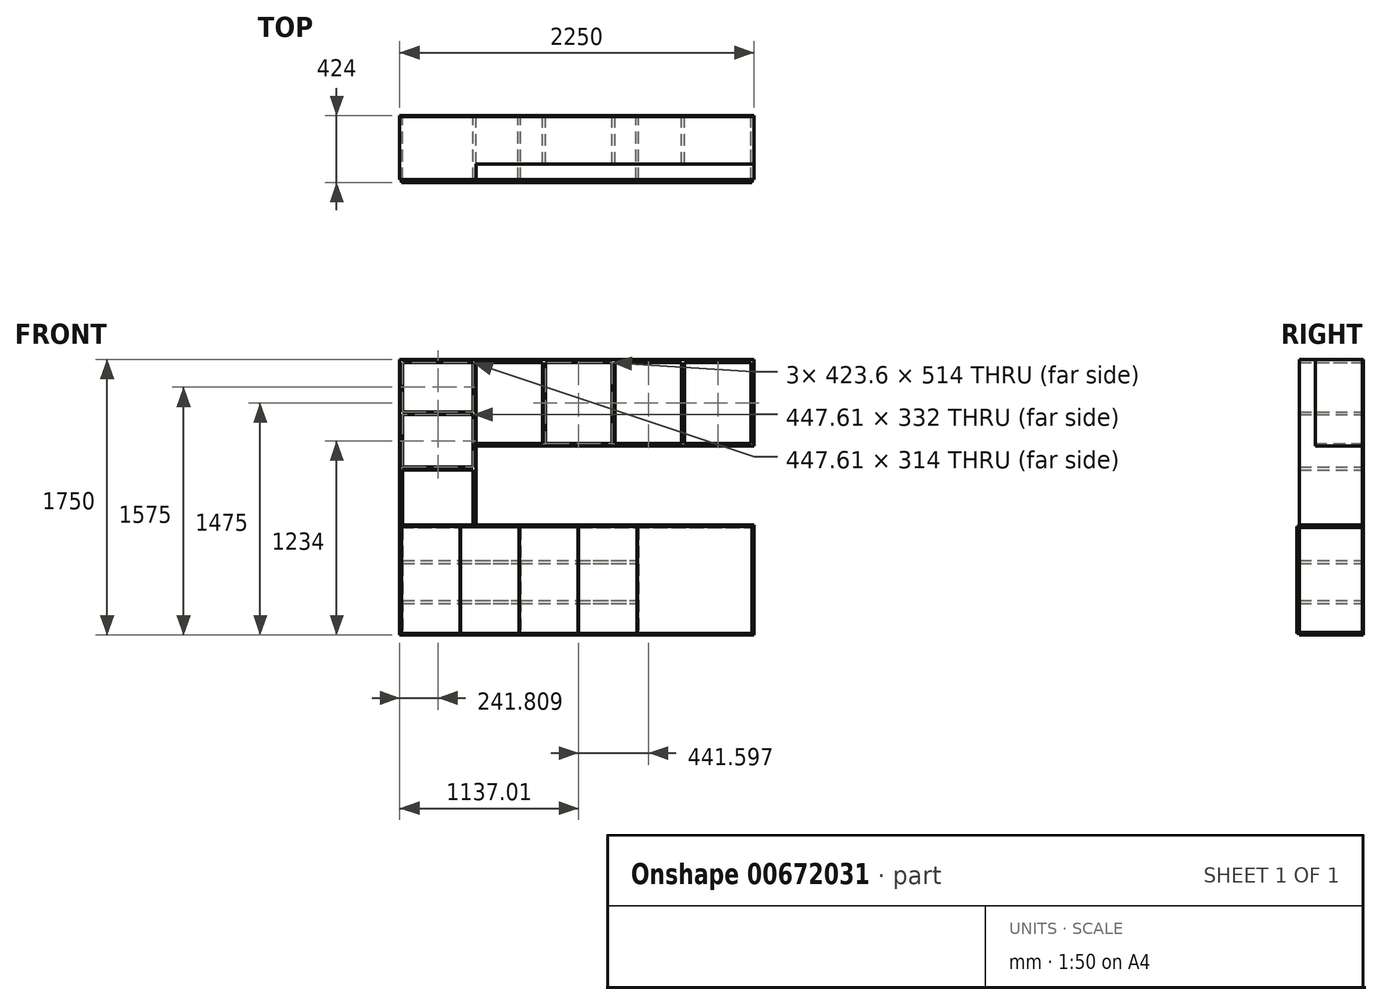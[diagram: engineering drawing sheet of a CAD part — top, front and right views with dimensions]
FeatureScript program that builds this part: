
annotation { "Feature Type Name" : "Feature", "Feature Type Description" : "" }
export const myFeature = defineFeature(function(context is Context, id is Id, definition is map)
    precondition{}
    {
        {
            var Q0;
            Q0=qCreatedBy(makeId("Front.planeOp"),FACE);
            var sketch = newSketch(context, id + "F0", { "sketchPlane" : qUnion([Q0])});
            skLineSegment(sketch, "E0.bottom", {"start": v(-1256.64, 283.33) * mm, "end": v(993.36, 283.33) * mm});
            skLineSegment(sketch, "E0.top", {"start": v(-1256.64, -416.67) * mm, "end": v(993.36, -416.67) * mm});
            skLineSegment(sketch, "E0.left", {"start": v(-1256.64, 283.33) * mm, "end": v(-1256.64, -416.67) * mm});
            skLineSegment(sketch, "E0.right", {"start": v(993.36, 283.33) * mm, "end": v(993.36, -416.67) * mm});
            skLineSegment(sketch, "E1.0", {"start": v(-1238.64, 265.33) * mm, "end": v(-1238.64, -398.67) * mm});
            skLineSegment(sketch, "E2.0", {"start": v(975.36, 265.33) * mm, "end": v(975.36, -398.67) * mm});
            skLineSegment(sketch, "E3.0", {"start": v(-1256.64, -398.67) * mm, "end": v(975.36, -398.67) * mm});
            skLineSegment(sketch, "E4.0", {"start": v(-1256.64, 265.33) * mm, "end": v(975.36, 265.33) * mm});
            skLineSegment(sketch, "E5", {"start": v(243.36, 265.33) * mm, "end": v(243.36, -398.67) * mm});
            skLineSegment(sketch, "E6.0", {"start": v(261.36, 265.33) * mm, "end": v(261.36, -398.67) * mm});
            skLineSegment(sketch, "E7", {"start": v(-1238.64, 57.6) * mm, "end": v(-506.64, 57.6) * mm});
            skLineSegment(sketch, "E8", {"start": v(-1238.64, -197.11) * mm, "end": v(-506.64, -197.11) * mm});
            skLineSegment(sketch, "E9", {"start": v(-506.64, 265.33) * mm, "end": v(-506.64, 265.33) * mm});
            skLineSegment(sketch, "E10", {"start": v(-506.64, 265.33) * mm, "end": v(-506.64, -398.67) * mm});
            skLineSegment(sketch, "E11.0", {"start": v(-488.64, 265.33) * mm, "end": v(-488.64, -398.67) * mm});
            skLineSegment(sketch, "E12.0", {"start": v(-1238.64, 39.6) * mm, "end": v(-506.64, 39.6) * mm});
            skLineSegment(sketch, "E13.0", {"start": v(-1238.64, -215.11) * mm, "end": v(-506.64, -215.11) * mm});
            skLineSegment(sketch, "E14.trimOffspring", {"start": v(-488.64, 57.6) * mm, "end": v(243.36, 57.6) * mm});
            skLineSegment(sketch, "E15.trimOffspring", {"start": v(-488.64, 39.6) * mm, "end": v(243.36, 39.6) * mm});
            skLineSegment(sketch, "E16.trimOffspring", {"start": v(-488.64, -197.11) * mm, "end": v(243.36, -197.11) * mm});
            skLineSegment(sketch, "E17.trimOffspring", {"start": v(-488.64, -215.11) * mm, "end": v(243.36, -215.11) * mm});
            skLineSegment(sketch, "E18", {"start": v(975.36, 265.33) * mm, "end": v(993.36, 265.33) * mm});
            skLineSegment(sketch, "E19", {"start": v(975.36, -398.67) * mm, "end": v(993.36, -398.67) * mm});
            skSolve(sketch);
        }
        {
            var Q0;
            {var subQ4=sQuery(id+"F0.wireOp",EDGE,"E0.bottom");Q0=makeQuery(id+"F0.imprint","IMPRINT",FACE,{"disambiguationData":[TD([[makeQuery(id+"F0.imprint","IMPRINT",EDGE,{"derivedFrom":subQ4}),-1.0]])]});}
            extrude(context, id + "F1", {"entities" : qUnion([Q0]), "depth" : 400 * mm, "offsetDistance" : 25 * mm});
        }
        {
            var Q0;
            {var subQ1=sQuery(id+"F0.wireOp",EDGE,"E0.top");Q0=makeQuery(id+"F0.imprint","IMPRINT",FACE,{"disambiguationData":[TD([[makeQuery(id+"F0.imprint","IMPRINT",EDGE,{"derivedFrom":subQ1}),1.0]])]});}
            extrude(context, id + "F2", {"entities" : qUnion([Q0]), "depth" : 400 * mm, "offsetDistance" : 25 * mm});
        }
        {
            var Q0;
            {var subQ5=sQuery(id+"F0.wireOp",EDGE,"E0.left");var subQ8=sQuery(id+"F0.wireOp",EDGE,"E3.0");var subQ9=makeQuery(id+"F0.imprint","INTERSECT",VERTEX,{"derivedFrom":[subQ5,subQ8]});Q0=makeQuery(id+"F0.imprint","IMPRINT",FACE,{"disambiguationData":[TD([[makeQuery(id+"F0.imprint","IMPRINT",EDGE,{"disambiguationData":[TD([[subQ9,1.0]])],"derivedFrom":subQ5}),1.0]])]});}
            extrude(context, id + "F3", {"entities" : qUnion([Q0]), "depth" : 400 * mm, "offsetDistance" : 25 * mm});
        }
        {
            var Q0;
            {var subQ5=sQuery(id+"F0.wireOp",EDGE,"E2.0");Q0=makeQuery(id+"F0.imprint","IMPRINT",FACE,{"disambiguationData":[TD([[makeQuery(id+"F0.imprint","IMPRINT",EDGE,{"derivedFrom":subQ5}),1.0]])]});}
            extrude(context, id + "F4", {"entities" : qUnion([Q0]), "depth" : 400 * mm, "offsetDistance" : 25 * mm});
        }
        {
            var Q0;
            {var subQ6=sQuery(id+"F0.wireOp",EDGE,"E10");var subQ7=sQuery(id+"F0.wireOp",EDGE,"E3.0");var subQ8=makeQuery(id+"F0.imprint","INTERSECT",VERTEX,{"derivedFrom":[subQ7,subQ6]});Q0=makeQuery(id+"F0.imprint","IMPRINT",FACE,{"disambiguationData":[TD([[makeQuery(id+"F0.imprint","IMPRINT",EDGE,{"disambiguationData":[TD([[subQ8,-1.0]])],"derivedFrom":subQ7}),1.0]])]});}
            extrude(context, id + "F5", {"entities" : qUnion([Q0]), "depth" : 400 * mm, "offsetDistance" : 25 * mm});
        }
        {
            var Q0;
            {var subQ0=sQuery(id+"F0.wireOp",EDGE,"E8");Q0=makeQuery(id+"F0.imprint","IMPRINT",FACE,{"disambiguationData":[TD([[makeQuery(id+"F0.imprint","IMPRINT",EDGE,{"derivedFrom":subQ0}),-1.0]])]});}
            extrude(context, id + "F6", {"entities" : qUnion([Q0]), "depth" : 400 * mm, "offsetDistance" : 25 * mm});
        }
        {
            var Q0;
            {var subQ0=sQuery(id+"F0.wireOp",EDGE,"E7");Q0=makeQuery(id+"F0.imprint","IMPRINT",FACE,{"disambiguationData":[TD([[makeQuery(id+"F0.imprint","IMPRINT",EDGE,{"derivedFrom":subQ0}),-1.0]])]});}
            extrude(context, id + "F7", {"entities" : qUnion([Q0]), "depth" : 400 * mm, "offsetDistance" : 25 * mm});
        }
        {
            var Q0;
            {var subQ0=sQuery(id+"F0.wireOp",EDGE,"E14.trimOffspring");Q0=makeQuery(id+"F0.imprint","IMPRINT",FACE,{"disambiguationData":[TD([[makeQuery(id+"F0.imprint","IMPRINT",EDGE,{"derivedFrom":subQ0}),-1.0]])]});}
            extrude(context, id + "F8", {"entities" : qUnion([Q0]), "depth" : 400 * mm, "offsetDistance" : 25 * mm});
        }
        {
            var Q0;
            {var subQ0=sQuery(id+"F0.wireOp",EDGE,"E16.trimOffspring");Q0=makeQuery(id+"F0.imprint","IMPRINT",FACE,{"disambiguationData":[TD([[makeQuery(id+"F0.imprint","IMPRINT",EDGE,{"derivedFrom":subQ0}),-1.0]])]});}
            extrude(context, id + "F9", {"entities" : qUnion([Q0]), "depth" : 400 * mm, "offsetDistance" : 25 * mm});
        }
        {
            var Q0;
            {var subQ5=sQuery(id+"F0.wireOp",EDGE,"E6.0");Q0=makeQuery(id+"F0.imprint","IMPRINT",FACE,{"disambiguationData":[TD([[makeQuery(id+"F0.imprint","IMPRINT",EDGE,{"derivedFrom":subQ5}),-1.0]])]});}
            extrude(context, id + "F10", {"entities" : qUnion([Q0]), "depth" : 400 * mm, "offsetDistance" : 25 * mm});
        }
        {
            var Q0;
            Q0=makeQuery(id+"F1.opExtrude","CAP_FACE",FACE,{"disambiguationData":[OSD([sQuery(id+"F0.wireOp",EDGE,"E0.bottom"),sQuery(id+"F0.wireOp",EDGE,"E0.left"),sQuery(id+"F0.wireOp",EDGE,"E0.right"),sQuery(id+"F0.wireOp",EDGE,"E4.0"),sQuery(id+"F0.wireOp",EDGE,"E18")])],"isStart":true});
            var sketch = newSketch(context, id + "F11", { "sketchPlane" : qUnion([Q0])});
            skLineSegment(sketch, "E20.bottom", {"start": v(-993.36, 283.33) * mm, "end": v(1256.64, 283.33) * mm});
            skLineSegment(sketch, "E20.top", {"start": v(-993.36, -416.67) * mm, "end": v(1256.64, -416.67) * mm});
            skLineSegment(sketch, "E20.left", {"start": v(1256.64, 283.33) * mm, "end": v(1256.64, -416.67) * mm});
            skLineSegment(sketch, "E20.right", {"start": v(-993.36, 283.33) * mm, "end": v(-993.36, -416.67) * mm});
            skSolve(sketch);
        }
        {
            var Q0;
            Q0 = qSketchRegion(id + "F11", true);
            extrude(context, id + "F12", {"entities" : qUnion([Q0]), "depth" : 6 * mm, "offsetDistance" : 25 * mm});
        }
        {
            var Q0;
            Q0=makeQuery(id+"F3.opExtrude","CAP_FACE",FACE,{"disambiguationData":[OSD([sQuery(id+"F0.wireOp",EDGE,"E0.left"),sQuery(id+"F0.wireOp",EDGE,"E1.0"),sQuery(id+"F0.wireOp",EDGE,"E3.0"),sQuery(id+"F0.wireOp",EDGE,"E4.0")])],"isStart":false});
            var sketch = newSketch(context, id + "F13", { "sketchPlane" : qUnion([Q0])});
            skLineSegment(sketch, "E21.0.1", {"start": v(993.36, 265.33) * mm, "end": v(993.36, 283.33) * mm});
            skPoint(sketch, "E22.0", {"position": v(-1238.64, 265.33) * mm});
            skPoint(sketch, "E22.1", {"position": v(-506.64, -398.67) * mm});
            skPoint(sketch, "E22.2", {"position": v(-1238.64, -398.67) * mm});
            skLineSegment(sketch, "E23.bottom", {"start": v(-1238.64, 265.33) * mm, "end": v(-506.64, 265.33) * mm, "construction": true});
            skLineSegment(sketch, "E23.top", {"start": v(-1238.64, -398.67) * mm, "end": v(-506.64, -398.67) * mm, "construction": true});
            skLineSegment(sketch, "E23.right", {"start": v(-506.64, 265.33) * mm, "end": v(-506.64, -398.67) * mm, "construction": true});
            skLineSegment(sketch, "E24.0", {"start": v(-1244.99, 271.68) * mm, "end": v(-874.23, 271.68) * mm});
            skLineSegment(sketch, "E24.1", {"start": v(-1244.99, 271.68) * mm, "end": v(-1244.99, -405.02) * mm});
            skLineSegment(sketch, "E24.2", {"start": v(-1244.99, -405.02) * mm, "end": v(-874.23, -405.02) * mm});
            skLineSegment(sketch, "E24.3", {"start": v(-500.29, 271.68) * mm, "end": v(-500.29, -405.02) * mm});
            skPoint(sketch, "E25.0", {"position": v(-488.64, -398.67) * mm});
            skPoint(sketch, "E25.1", {"position": v(243.36, -398.67) * mm});
            skPoint(sketch, "E25.2", {"position": v(-488.64, 265.33) * mm});
            skLineSegment(sketch, "E26.bottom", {"start": v(-488.64, 265.33) * mm, "end": v(243.36, 265.33) * mm, "construction": true});
            skLineSegment(sketch, "E26.top", {"start": v(-488.64, -398.67) * mm, "end": v(243.36, -398.67) * mm, "construction": true});
            skLineSegment(sketch, "E26.left", {"start": v(-488.64, 265.33) * mm, "end": v(-488.64, -398.67) * mm, "construction": true});
            skLineSegment(sketch, "E26.right", {"start": v(243.36, 265.33) * mm, "end": v(243.36, -398.67) * mm, "construction": true});
            skLineSegment(sketch, "E27.0", {"start": v(-494.99, 271.68) * mm, "end": v(-494.99, -405.02) * mm});
            skLineSegment(sketch, "E27.1", {"start": v(-494.99, 271.68) * mm, "end": v(-122.64, 271.68) * mm});
            skLineSegment(sketch, "E27.2", {"start": v(249.71, 271.68) * mm, "end": v(249.71, -405.02) * mm});
            skLineSegment(sketch, "E27.3", {"start": v(-494.99, -405.02) * mm, "end": v(-124.23, -405.02) * mm});
            skLineSegment(sketch, "E28", {"start": v(-122.64, 271.68) * mm, "end": v(249.71, 271.68) * mm});
            skLineSegment(sketch, "E29", {"start": v(-121.05, -405.02) * mm, "end": v(249.71, -405.02) * mm});
            skLineSegment(sketch, "E30", {"start": v(-871.05, -405.02) * mm, "end": v(-500.29, -405.02) * mm});
            skLineSegment(sketch, "E31", {"start": v(-871.05, 271.68) * mm, "end": v(-500.29, 271.68) * mm});
            skLineSegment(sketch, "E32", {"start": v(-122.64, 271.68) * mm, "end": v(-122.64, 265.33) * mm});
            skLineSegment(sketch, "E33.0", {"start": v(-874.23, -405.02) * mm, "end": v(-874.23, 271.68) * mm});
            skLineSegment(sketch, "E34.0", {"start": v(-871.05, -405.02) * mm, "end": v(-871.05, 271.68) * mm});
            skLineSegment(sketch, "E35.0", {"start": v(-124.23, 271.68) * mm, "end": v(-124.23, -405.02) * mm});
            skLineSegment(sketch, "E36.0", {"start": v(-121.05, 271.68) * mm, "end": v(-121.05, -405.02) * mm});
            skPoint(sketch, "E37.orphan", {"position": v(-122.64, -405.02) * mm});
            skSolve(sketch);
        }
        {
            var Q0;
            Q0 = qSketchRegion(id + "F13", true);
            extrude(context, id + "F14", {"entities" : qUnion([Q0]), "depth" : 18 * mm, "offsetDistance" : 25 * mm});
        }
        {
            var Q0;
            Q0=makeQuery(id+"F4.opExtrude","CAP_FACE",FACE,{"disambiguationData":[OSD([sQuery(id+"F0.wireOp",EDGE,"E0.right"),sQuery(id+"F0.wireOp",EDGE,"E2.0"),sQuery(id+"F0.wireOp",EDGE,"E18"),sQuery(id+"F0.wireOp",EDGE,"E19")])],"isStart":false});
            var sketch = newSketch(context, id + "F15", { "sketchPlane" : qUnion([Q0])});
            skPoint(sketch, "E38.0", {"position": v(261.36, 265.33) * mm});
            skPoint(sketch, "E38.1", {"position": v(975.36, 265.33) * mm});
            skLineSegment(sketch, "E39.bottom", {"start": v(261.36, 265.33) * mm, "end": v(975.36, 265.33) * mm, "construction": true});
            skLineSegment(sketch, "E39.right", {"start": v(975.36, 265.33) * mm, "end": v(975.36, -358.87) * mm});
            skPoint(sketch, "E40.0", {"position": v(975.36, -398.67) * mm});
            skLineSegment(sketch, "E41.bottom", {"start": v(261.36, 265.33) * mm, "end": v(975.36, 265.33) * mm});
            skLineSegment(sketch, "E41.top", {"start": v(261.36, -398.67) * mm, "end": v(975.36, -398.67) * mm});
            skLineSegment(sketch, "E41.left", {"start": v(261.36, 265.33) * mm, "end": v(261.36, -398.67) * mm, "construction": true});
            skLineSegment(sketch, "E41.right", {"start": v(975.36, 265.33) * mm, "end": v(975.36, -398.67) * mm});
            skLineSegment(sketch, "E42.top", {"start": v(261.36, -398.67) * mm, "end": v(975.36, -398.67) * mm, "construction": true});
            skLineSegment(sketch, "E42.right", {"start": v(975.36, 265.33) * mm, "end": v(975.36, -398.67) * mm, "construction": true});
            skLineSegment(sketch, "E43.0", {"start": v(255.01, 271.68) * mm, "end": v(255.01, -405.02) * mm});
            skLineSegment(sketch, "E43.1", {"start": v(255.01, 271.68) * mm, "end": v(981.71, 271.68) * mm});
            skLineSegment(sketch, "E43.2", {"start": v(981.71, 271.68) * mm, "end": v(981.71, -405.02) * mm});
            skLineSegment(sketch, "E43.3", {"start": v(255.01, -405.02) * mm, "end": v(981.71, -405.02) * mm});
            skSolve(sketch);
        }
        {
            var Q0;
            Q0 = qSketchRegion(id + "F15", true);
            extrude(context, id + "F16", {"entities" : qUnion([Q0]), "depth" : 18 * mm, "offsetDistance" : 25 * mm});
        }
        {
            var Q0;
            Q0=makeQuery(id+"F12.opExtrude","CAP_FACE",FACE,{"disambiguationData":[OSD([sQuery(id+"F11.wireOp",EDGE,"E20.bottom"),sQuery(id+"F11.wireOp",EDGE,"E20.top"),sQuery(id+"F11.wireOp",EDGE,"E20.right"),sQuery(id+"F11.wireOp",EDGE,"E20.left")])],"isStart":true});
            var sketch = newSketch(context, id + "F17", { "sketchPlane" : qUnion([Q0])});
            skLineSegment(sketch, "E44", {"start": v(-1256.64, 283.33) * mm, "end": v(-1256.64, 630.88) * mm});
            skLineSegment(sketch, "E45", {"start": v(-1256.64, 1333.33) * mm, "end": v(-773.02, 1333.33) * mm});
            skLineSegment(sketch, "E46", {"start": v(993.36, 1333.33) * mm, "end": v(993.36, 283.33) * mm});
            skLineSegment(sketch, "E47", {"start": v(-773.02, 1315.33) * mm, "end": v(-773.02, 301.33) * mm});
            skLineSegment(sketch, "E48", {"start": v(-1238.64, 633.33) * mm, "end": v(-791.02, 633.33) * mm});
            skLineSegment(sketch, "E49", {"start": v(-1256.64, 983.33) * mm, "end": v(-1256.64, 983.33) * mm});
            skLineSegment(sketch, "E50", {"start": v(993.36, 783.33) * mm, "end": v(110.17, 783.33) * mm});
            skLineSegment(sketch, "E51", {"start": v(-773.02, 1333.33) * mm, "end": v(110.17, 1333.33) * mm});
            skLineSegment(sketch, "E52", {"start": v(110.17, 1315.33) * mm, "end": v(110.17, 801.33) * mm});
            skLineSegment(sketch, "E53", {"start": v(110.17, 1333.33) * mm, "end": v(993.36, 1333.33) * mm});
            skLineSegment(sketch, "E54", {"start": v(110.17, 783.33) * mm, "end": v(-773.02, 783.33) * mm});
            skLineSegment(sketch, "E55", {"start": v(551.77, 1315.33) * mm, "end": v(551.77, 801.33) * mm});
            skLineSegment(sketch, "E56", {"start": v(-331.43, 1315.33) * mm, "end": v(-331.43, 801.33) * mm});
            skLineSegment(sketch, "E57", {"start": v(-1256.64, 630.88) * mm, "end": v(-1256.64, 1333.33) * mm});
            skLineSegment(sketch, "E58", {"start": v(-1238.64, 983.33) * mm, "end": v(-791.02, 983.33) * mm});
            skLineSegment(sketch, "E59", {"start": v(-773.02, 633.33) * mm, "end": v(-773.02, 633.33) * mm});
            skLineSegment(sketch, "E60.0", {"start": v(-1238.64, 1315.33) * mm, "end": v(-791.02, 1315.33) * mm});
            skLineSegment(sketch, "E61.0", {"start": v(-1238.64, 630.88) * mm, "end": v(-1238.64, 1333.33) * mm});
            skLineSegment(sketch, "E62.0", {"start": v(-1238.64, 1001.33) * mm, "end": v(-791.02, 1001.33) * mm});
            skLineSegment(sketch, "E63.0", {"start": v(-1238.64, 651.33) * mm, "end": v(-791.02, 651.33) * mm});
            skLineSegment(sketch, "E64.0", {"start": v(-1238.64, 283.33) * mm, "end": v(-1238.64, 630.88) * mm});
            skLineSegment(sketch, "E65.0", {"start": v(-791.02, 1315.33) * mm, "end": v(-791.02, 301.33) * mm});
            skLineSegment(sketch, "E66.0", {"start": v(-349.43, 1315.33) * mm, "end": v(-349.43, 801.33) * mm});
            skLineSegment(sketch, "E67.0", {"start": v(-773.02, 1315.33) * mm, "end": v(110.17, 1315.33) * mm});
            skLineSegment(sketch, "E68.0", {"start": v(110.17, 801.33) * mm, "end": v(-773.02, 801.33) * mm});
            skLineSegment(sketch, "E69.0", {"start": v(92.17, 1315.33) * mm, "end": v(92.17, 801.33) * mm});
            skLineSegment(sketch, "E70.0", {"start": v(533.77, 1315.33) * mm, "end": v(533.77, 801.33) * mm});
            skLineSegment(sketch, "E71.0", {"start": v(975.36, 1315.33) * mm, "end": v(975.36, 801.33) * mm});
            skLineSegment(sketch, "E72.0", {"start": v(110.17, 1315.33) * mm, "end": v(993.36, 1315.33) * mm});
            skLineSegment(sketch, "E73.0", {"start": v(993.36, 801.33) * mm, "end": v(110.17, 801.33) * mm});
            skPoint(sketch, "E74.orphan", {"position": v(-1256.64, 633.33) * mm});
            skLineSegment(sketch, "E75.trimOffspring", {"start": v(975.36, 301.33) * mm, "end": v(993.36, 301.33) * mm});
            skPoint(sketch, "E76.orphan", {"position": v(-773.02, 983.33) * mm});
            skPoint(sketch, "E77.orphan", {"position": v(551.77, 1333.33) * mm});
            skLineSegment(sketch, "E78.trimOffspring", {"start": v(975.36, 783.33) * mm, "end": v(975.36, 283.33) * mm});
            skLineSegment(sketch, "E79", {"start": v(-791.02, 301.33) * mm, "end": v(-791.02, 283.33) * mm});
            skLineSegment(sketch, "E80", {"start": v(-773.02, 301.33) * mm, "end": v(-773.02, 283.33) * mm});
            skLineSegment(sketch, "E81", {"start": v(-791.02, 1315.33) * mm, "end": v(-791.02, 1333.33) * mm});
            skLineSegment(sketch, "E82", {"start": v(-773.02, 1315.33) * mm, "end": v(-773.02, 1333.33) * mm});
            skSolve(sketch);
        }
        {
            var Q0;
            {var subQ8=sQuery(id+"F17.wireOp",EDGE,"E44");Q0=makeQuery(id+"F17.imprint","IMPRINT",FACE,{"disambiguationData":[TD([[makeQuery(id+"F17.imprint","IMPRINT",EDGE,{"derivedFrom":subQ8}),-1.0]])]});}
            var Q1;
            {var subQ4=sQuery(id+"F17.wireOp",EDGE,"E60.0");Q1=makeQuery(id+"F17.imprint","IMPRINT",FACE,{"disambiguationData":[TD([[makeQuery(id+"F17.imprint","IMPRINT",EDGE,{"derivedFrom":subQ4}),1.0]])]});}
            var Q2;
            {var subQ0=sQuery(id+"F17.wireOp",EDGE,"E79");Q2=makeQuery(id+"F17.imprint","IMPRINT",FACE,{"disambiguationData":[TD([[makeQuery(id+"F17.imprint","IMPRINT",EDGE,{"derivedFrom":subQ0}),1.0]])]});}
            var Q3;
            {var subQ0=sQuery(id+"F17.wireOp",EDGE,"E58");Q3=makeQuery(id+"F17.imprint","IMPRINT",FACE,{"disambiguationData":[TD([[makeQuery(id+"F17.imprint","IMPRINT",EDGE,{"derivedFrom":subQ0}),1.0]])]});}
            var Q4;
            {var subQ0=sQuery(id+"F17.wireOp",EDGE,"E48");Q4=makeQuery(id+"F17.imprint","IMPRINT",FACE,{"disambiguationData":[TD([[makeQuery(id+"F17.imprint","IMPRINT",EDGE,{"derivedFrom":subQ0}),1.0]])]});}
            extrude(context, id + "F18", {"entities" : qUnion([Q0, Q1, Q2, Q3, Q4]), "operationType" : NewBodyOperationType.ADD, "depth" : 400 * mm, "offsetDistance" : 25 * mm});
        }
        {
            var Q0;
            Q0=makeQuery(id+"F17.imprint","IMPRINT",FACE,{"disambiguationData":[TD([[makeQuery(id+"F17.imprint","IMPRINT",EDGE,{"derivedFrom":sQuery(id+"F17.wireOp",EDGE,"E51")}),-1.0]])]});
            var Q1;
            {var subQ4=sQuery(id+"F17.wireOp",EDGE,"E54");Q1=makeQuery(id+"F17.imprint","IMPRINT",FACE,{"disambiguationData":[TD([[makeQuery(id+"F17.imprint","IMPRINT",EDGE,{"derivedFrom":subQ4}),-1.0]])]});}
            var Q2;
            {var subQ0=sQuery(id+"F17.wireOp",EDGE,"E56");Q2=makeQuery(id+"F17.imprint","IMPRINT",FACE,{"disambiguationData":[TD([[makeQuery(id+"F17.imprint","IMPRINT",EDGE,{"derivedFrom":subQ0}),-1.0]])]});}
            var Q3;
            {var subQ0=sQuery(id+"F17.wireOp",EDGE,"E52");Q3=makeQuery(id+"F17.imprint","IMPRINT",FACE,{"disambiguationData":[TD([[makeQuery(id+"F17.imprint","IMPRINT",EDGE,{"derivedFrom":subQ0}),-1.0]])]});}
            var Q4;
            {var subQ0=sQuery(id+"F17.wireOp",EDGE,"E55");Q4=makeQuery(id+"F17.imprint","IMPRINT",FACE,{"disambiguationData":[TD([[makeQuery(id+"F17.imprint","IMPRINT",EDGE,{"derivedFrom":subQ0}),-1.0]])]});}
            var Q5;
            {var subQ5=sQuery(id+"F17.wireOp",EDGE,"E71.0");Q5=makeQuery(id+"F17.imprint","IMPRINT",FACE,{"disambiguationData":[TD([[makeQuery(id+"F17.imprint","IMPRINT",EDGE,{"derivedFrom":subQ5}),1.0]])]});}
            extrude(context, id + "F19", {"entities" : qUnion([Q0, Q1, Q2, Q3, Q4, Q5]), "operationType" : NewBodyOperationType.ADD, "depth" : 300 * mm, "offsetDistance" : 25 * mm});
        }
        {
            var Q0;
            {var subQ0=sQuery(id+"F17.wireOp",EDGE,"E82");var subQ1=sQuery(id+"F17.wireOp",EDGE,"E47");Q0=makeQuery(id+"F19.boolean.opBoolean","MERGE",FACE,{"derivedFrom":[makeQuery(id+"F18.boolean.opBoolean","MERGE",FACE,{"derivedFrom":[makeQuery(id+"F1.opExtrude","CAP_FACE",FACE,{"disambiguationData":[OSD([sQuery(id+"F0.wireOp",EDGE,"E0.bottom"),sQuery(id+"F0.wireOp",EDGE,"E0.left"),sQuery(id+"F0.wireOp",EDGE,"E0.right"),sQuery(id+"F0.wireOp",EDGE,"E4.0"),sQuery(id+"F0.wireOp",EDGE,"E18")])],"isStart":true}),makeQuery(id+"F18.opExtrude","CAP_FACE",FACE,{"disambiguationData":[OSD([sQuery(id+"F11.wireOp",EDGE,"E20.bottom"),sQuery(id+"F17.wireOp",EDGE,"E44"),sQuery(id+"F17.wireOp",EDGE,"E45"),subQ1,sQuery(id+"F17.wireOp",EDGE,"E48"),sQuery(id+"F17.wireOp",EDGE,"E57"),sQuery(id+"F17.wireOp",EDGE,"E58"),sQuery(id+"F17.wireOp",EDGE,"E60.0"),sQuery(id+"F17.wireOp",EDGE,"E61.0"),sQuery(id+"F17.wireOp",EDGE,"E62.0"),sQuery(id+"F17.wireOp",EDGE,"E63.0"),sQuery(id+"F17.wireOp",EDGE,"E64.0"),sQuery(id+"F17.wireOp",EDGE,"E65.0"),sQuery(id+"F17.wireOp",EDGE,"E79"),sQuery(id+"F17.wireOp",EDGE,"E80"),subQ0])],"isStart":true})]}),makeQuery(id+"F19.opExtrude","CAP_FACE",FACE,{"disambiguationData":[OSD([sQuery(id+"F17.wireOp",EDGE,"E46"),subQ1,sQuery(id+"F17.wireOp",EDGE,"E50"),sQuery(id+"F17.wireOp",EDGE,"E51"),sQuery(id+"F17.wireOp",EDGE,"E52"),sQuery(id+"F17.wireOp",EDGE,"E53"),sQuery(id+"F17.wireOp",EDGE,"E54"),sQuery(id+"F17.wireOp",EDGE,"E55"),sQuery(id+"F17.wireOp",EDGE,"E56"),sQuery(id+"F17.wireOp",EDGE,"E66.0"),sQuery(id+"F17.wireOp",EDGE,"E67.0"),sQuery(id+"F17.wireOp",EDGE,"E68.0"),sQuery(id+"F17.wireOp",EDGE,"E69.0"),sQuery(id+"F17.wireOp",EDGE,"E70.0"),sQuery(id+"F17.wireOp",EDGE,"E71.0"),sQuery(id+"F17.wireOp",EDGE,"E72.0"),sQuery(id+"F17.wireOp",EDGE,"E73.0"),subQ0])],"isStart":true})]});}
            var sketch = newSketch(context, id + "F20", { "sketchPlane" : qUnion([Q0])});
            skLineSegment(sketch, "E83", {"start": v(-993.36, 1333.33) * mm, "end": v(1256.64, 1333.33) * mm});
            skLineSegment(sketch, "E84", {"start": v(1256.64, 1333.33) * mm, "end": v(1238.64, 283.33) * mm});
            skLineSegment(sketch, "E85", {"start": v(1238.64, 283.33) * mm, "end": v(773.02, 283.33) * mm});
            skLineSegment(sketch, "E86", {"start": v(773.02, 283.33) * mm, "end": v(773.02, 783.33) * mm});
            skLineSegment(sketch, "E87", {"start": v(773.02, 783.33) * mm, "end": v(-993.36, 783.33) * mm});
            skLineSegment(sketch, "E88", {"start": v(-993.36, 783.33) * mm, "end": v(-993.36, 1333.33) * mm});
            skSolve(sketch);
        }
        {
            var Q0;
            Q0 = qSketchRegion(id + "F20", true);
            extrude(context, id + "F21", {"entities" : qUnion([Q0]), "depth" : 6 * mm, "offsetDistance" : 25 * mm});
        }
    });
